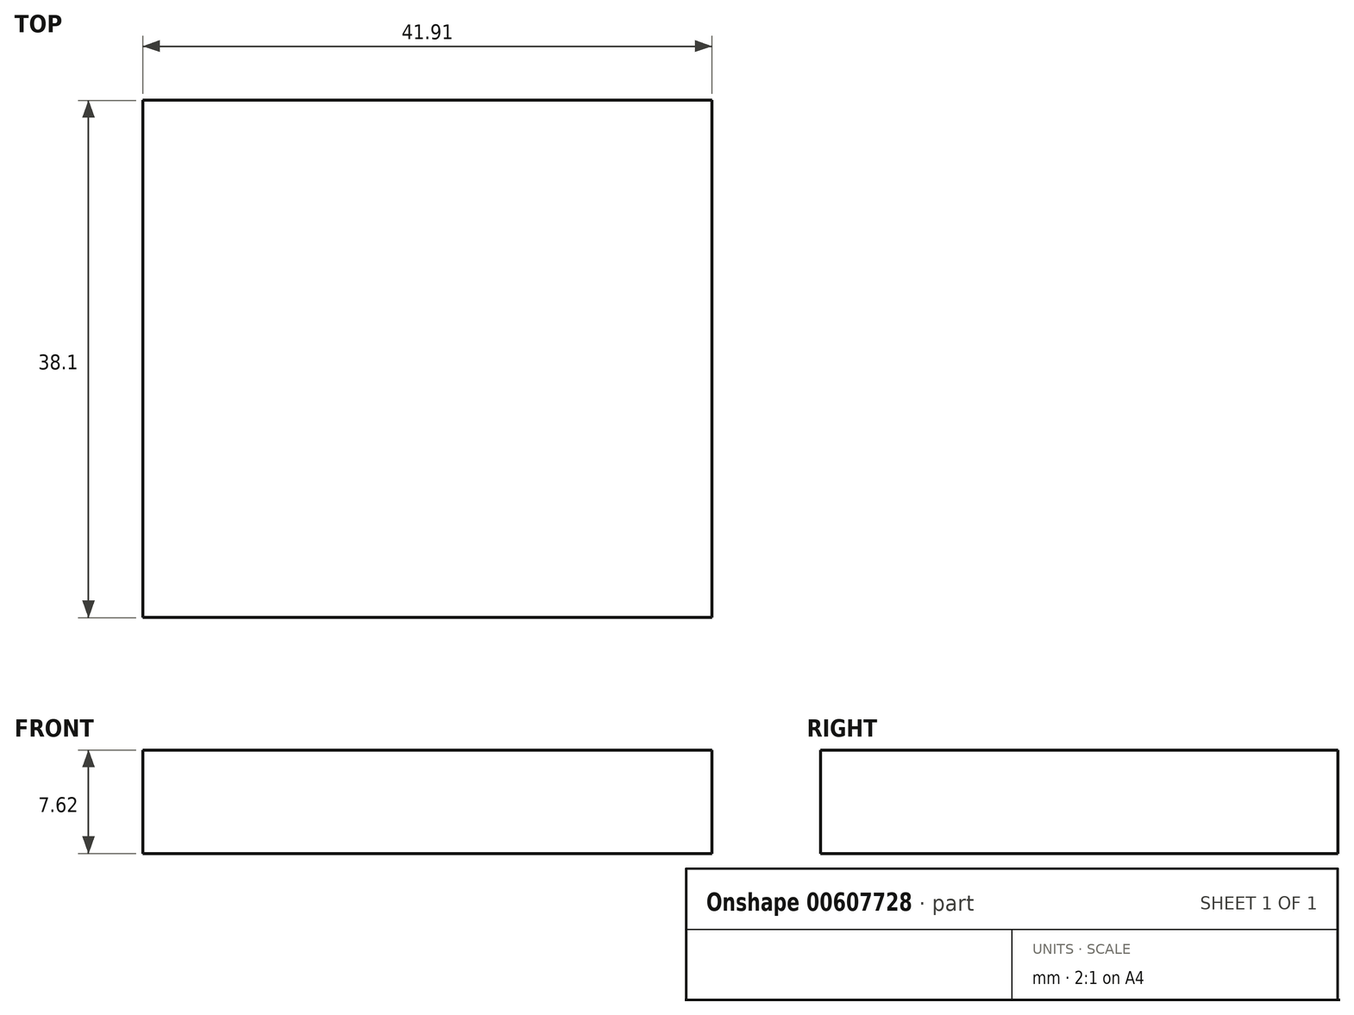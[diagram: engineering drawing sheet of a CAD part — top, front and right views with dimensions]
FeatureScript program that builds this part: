
annotation { "Feature Type Name" : "Feature", "Feature Type Description" : "" }
export const myFeature = defineFeature(function(context is Context, id is Id, definition is map)
    precondition{}
    {
        {
            var Q0;
            Q0=qCreatedBy(makeId("Top.planeOp"),FACE);
            var sketch = newSketch(context, id + "F0", { "sketchPlane" : qUnion([Q0])});
            skLineSegment(sketch, "E0.bottom", {"start": v(-68, -20.64) * mm, "end": v(-26.1, -20.64) * mm});
            skLineSegment(sketch, "E0.top", {"start": v(-68, 17.46) * mm, "end": v(-26.1, 17.46) * mm});
            skLineSegment(sketch, "E0.left", {"start": v(-68, -20.64) * mm, "end": v(-68, 17.46) * mm});
            skLineSegment(sketch, "E0.right", {"start": v(-26.1, -20.64) * mm, "end": v(-26.1, 17.46) * mm});
            skSolve(sketch);
        }
        {
            var Q0;
            Q0 = qSketchRegion(id + "F0", true);
            extrude(context, id + "F1", {"entities" : qUnion([Q0]), "depth" : 7.62 * mm, "offsetDistance" : 25.4 * mm});
        }
    });
